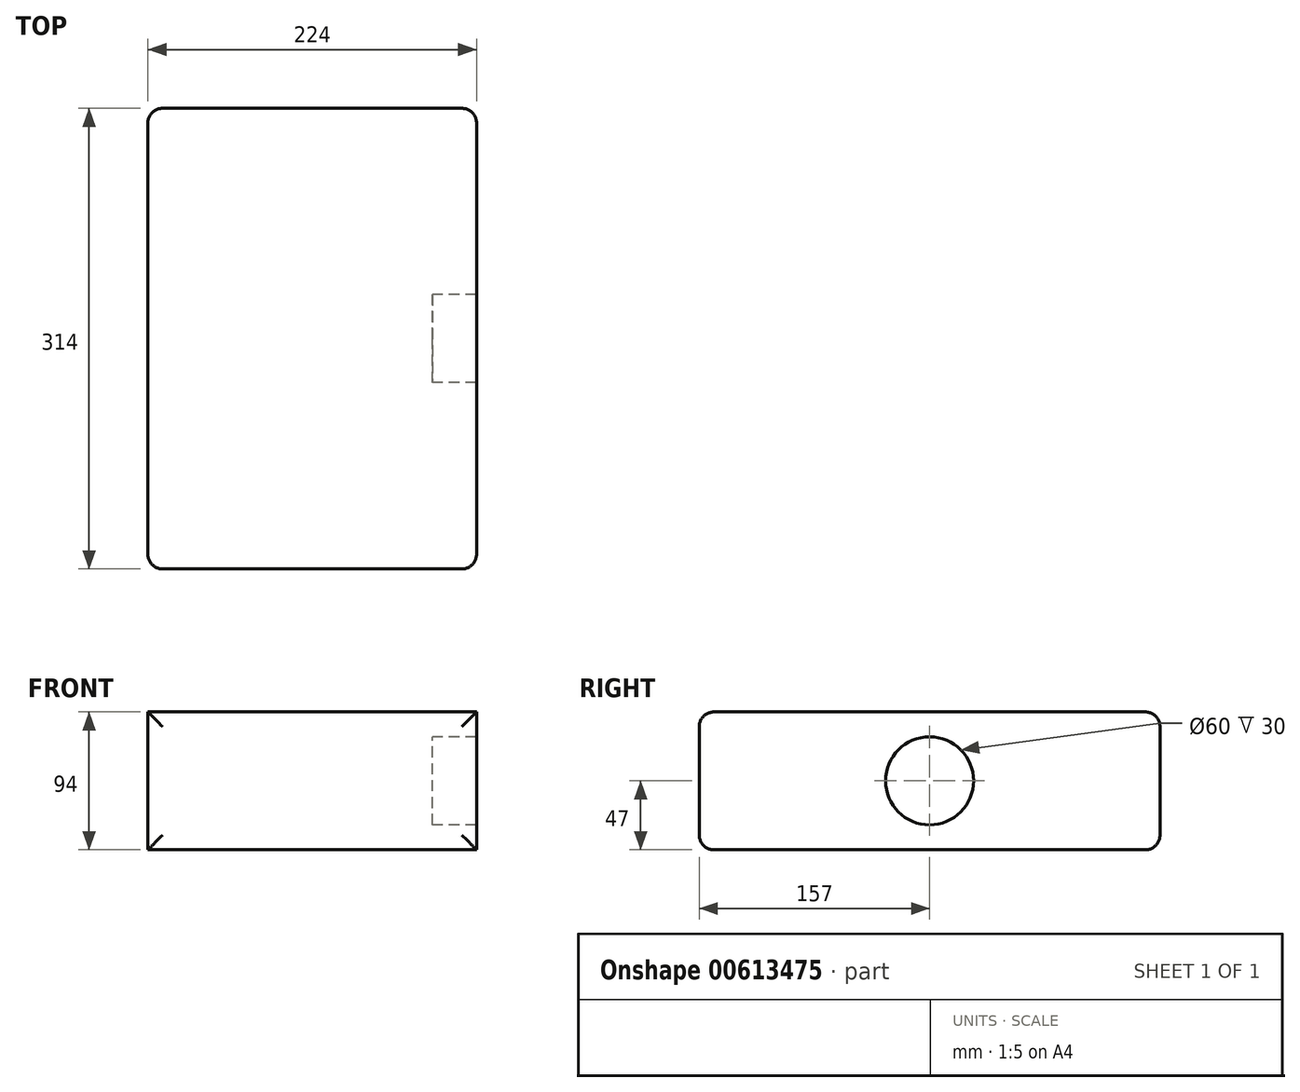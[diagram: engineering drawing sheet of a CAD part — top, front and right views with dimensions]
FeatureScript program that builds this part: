
annotation { "Feature Type Name" : "Feature", "Feature Type Description" : "" }
export const myFeature = defineFeature(function(context is Context, id is Id, definition is map)
    precondition{}
    {
        {
            var Q0;
            Q0=qCreatedBy(makeId("Front.planeOp"),FACE);
            var sketch = newSketch(context, id + "F0", { "sketchPlane" : qUnion([Q0])});
            skLineSegment(sketch, "E0.bottom", {"start": v(-112, -47) * mm, "end": v(112, -47) * mm});
            skLineSegment(sketch, "E0.top", {"start": v(-112, 47) * mm, "end": v(112, 47) * mm});
            skLineSegment(sketch, "E0.left", {"start": v(-112, -47) * mm, "end": v(-112, 47) * mm});
            skLineSegment(sketch, "E0.right", {"start": v(112, -47) * mm, "end": v(112, 47) * mm});
            skPoint(sketch, "E0.middle", {"position": v(0, 0) * mm});
            skSolve(sketch);
        }
        {
            var Q0;
            Q0 = qSketchRegion(id + "F0", true);
            extrude(context, id + "F1", {"entities" : qUnion([Q0]), "endBound" : BoundingType.SYMMETRIC, "depth" : 314 * mm, "offsetDistance" : 25 * mm});
        }
        {
            var Q0;
            Q0=makeQuery(id+"F1.opExtrude","CAP_FACE",FACE,{"disambiguationData":[OSD([sQuery(id+"F0.wireOp",EDGE,"E0.bottom"),sQuery(id+"F0.wireOp",EDGE,"E0.top"),sQuery(id+"F0.wireOp",EDGE,"E0.left"),sQuery(id+"F0.wireOp",EDGE,"E0.right")])],"isStart":false});
            fillet(context, id + "F2", {"entities" : qUnion([Q0]), "radius" : 10 * mm, "tangentPropagation" : true, "allowEdgeOverflow" : false});
        }
        {
            var Q0;
            Q0=makeQuery(id+"F1.opExtrude","CAP_FACE",FACE,{"disambiguationData":[OSD([sQuery(id+"F0.wireOp",EDGE,"E0.bottom"),sQuery(id+"F0.wireOp",EDGE,"E0.top"),sQuery(id+"F0.wireOp",EDGE,"E0.left"),sQuery(id+"F0.wireOp",EDGE,"E0.right")])],"isStart":true});
            fillet(context, id + "F3", {"entities" : qUnion([Q0]), "radius" : 10 * mm, "tangentPropagation" : true, "allowEdgeOverflow" : false});
        }
        {
            var Q0;
            Q0=makeQuery(id+"F1.opExtrude","SWEPT_FACE",FACE,{"disambiguationData":[OSD([sQuery(id+"F0.wireOp",EDGE,"E0.right")])]});
            cPlane(context, id + "F4", {"entities" : qUnion([Q0]), "cplaneType" : CPlaneType.OFFSET, "offset" : 30 * mm, "oppositeDirection" : true, "width" : 150 * mm, "height" : 150 * mm});
        }
        {
            var Q0;
            Q0=qCreatedBy(id+"F4.planeOp",FACE);
            var sketch = newSketch(context, id + "F5", { "sketchPlane" : qUnion([Q0])});
            skCircle(sketch, "E1", {"center": v(0, 0) * mm, "radius": 30 * mm});
            skSolve(sketch);
        }
        {
            var Q0;
            Q0 = qSketchRegion(id + "F5", true);
            extrude(context, id + "F6", {"entities" : qUnion([Q0]), "operationType" : NewBodyOperationType.REMOVE, "depth" : 30 * mm, "offsetDistance" : 25 * mm});
        }
    });
